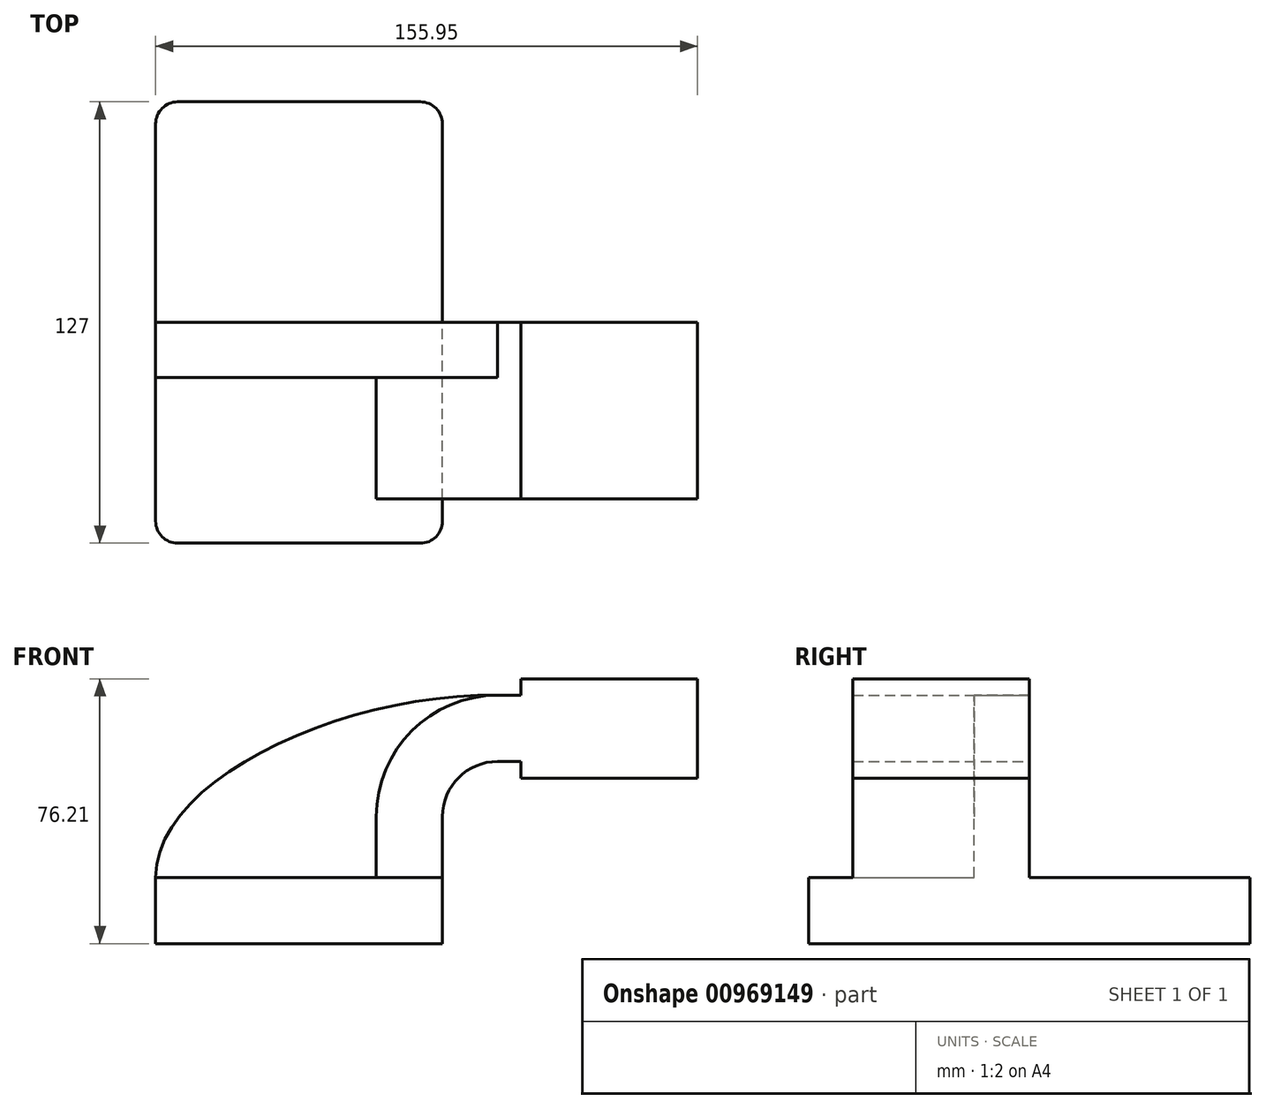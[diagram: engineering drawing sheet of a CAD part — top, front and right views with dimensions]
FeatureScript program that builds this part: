
annotation { "Feature Type Name" : "Feature", "Feature Type Description" : "" }
export const myFeature = defineFeature(function(context is Context, id is Id, definition is map)
    precondition{}
    {
        {
            var Q0;
            Q0=qCreatedBy(makeId("Front.planeOp"),FACE);
            var sketch = newSketch(context, id + "F0", { "sketchPlane" : qUnion([Q0])});
            skLineSegment(sketch, "E0.bottom", {"start": v(-41.27, -9.53) * mm, "end": v(41.28, -9.53) * mm});
            skLineSegment(sketch, "E0.top", {"start": v(-41.28, 9.53) * mm, "end": v(41.28, 9.53) * mm});
            skLineSegment(sketch, "E0.left", {"start": v(-41.28, -9.53) * mm, "end": v(-41.28, 9.53) * mm});
            skLineSegment(sketch, "E0.right", {"start": v(41.28, -9.53) * mm, "end": v(41.28, 9.52) * mm});
            skPoint(sketch, "E0.middle", {"position": v(0, 0) * mm});
            skLineSegment(sketch, "E1.bottom", {"start": v(63.87, 38.1) * mm, "end": v(114.67, 38.1) * mm});
            skLineSegment(sketch, "E1.top", {"start": v(63.87, 66.68) * mm, "end": v(114.67, 66.68) * mm});
            skLineSegment(sketch, "E1.left", {"start": v(63.87, 38.1) * mm, "end": v(63.87, 66.68) * mm});
            skLineSegment(sketch, "E1.right", {"start": v(114.67, 38.1) * mm, "end": v(114.67, 66.68) * mm});
            skPoint(sketch, "E1.middle", {"position": v(89.27, 52.39) * mm});
            skLineSegment(sketch, "E2", {"start": v(41.28, 9.52) * mm, "end": v(41.28, 27) * mm});
            skArc(sketch, "E3", {"start": v(41.27, 27) * mm, "mid": v(45.92, 38.23) * mm, "end": v(57.15, 42.88) * mm});
            skLineSegment(sketch, "E4", {"start": v(57.15, 42.88) * mm, "end": v(89.27, 42.88) * mm});
            skArc(sketch, "E5.0", {"start": v(53.97, 27) * mm, "mid": v(54.9, 29.25) * mm, "end": v(57.15, 30.18) * mm});
            skLineSegment(sketch, "E6.0", {"start": v(57.15, 61.93) * mm, "end": v(89.27, 61.93) * mm});
            skArc(sketch, "E6.1", {"start": v(22.22, 27) * mm, "mid": v(32.45, 51.7) * mm, "end": v(57.15, 61.93) * mm});
            skLineSegment(sketch, "E6.2", {"start": v(22.22, 9.52) * mm, "end": v(22.22, 27) * mm});
            skLineSegment(sketch, "E7", {"start": v(89.27, 66.68) * mm, "end": v(89.27, 38.1) * mm});
            skFitSpline(sketch, "E8", {"points": [v(-41.28, 9.53) * mm, v(57.15, 61.93) * mm], "startDerivative": vector(0.5, 85.92) * mm, "endDerivative": vector(132.47, -2.09) * mm});
            skPoint(sketch, "E9", {"position": v(114.67, 52.39) * mm});
            skPoint(sketch, "E10", {"position": v(63.87, 52.39) * mm});
            skSolve(sketch);
        }
        {
            var Q0;
            Q0=makeQuery(id+"F0.imprint","IMPRINT",FACE,{"disambiguationData":[TD([[makeQuery(id+"F0.imprint","IMPRINT",EDGE,{"derivedFrom":sQuery(id+"F0.wireOp",EDGE,"E0.bottom")}),1.0]])]});
            extrude(context, id + "F1", {"entities" : qUnion([Q0]), "endBound" : BoundingType.SYMMETRIC, "depth" : 127 * mm, "offsetDistance" : 25.4 * mm});
        }
        {
            var Q0;
            {var subQ1=sQuery(id+"F0.wireOp",EDGE,"E2");Q0=makeQuery(id+"F0.imprint","IMPRINT",FACE,{"disambiguationData":[TD([[makeQuery(id+"F0.imprint","IMPRINT",EDGE,{"derivedFrom":subQ1}),1.0]])]});}
            extrude(context, id + "F2", {"entities" : qUnion([Q0]), "operationType" : NewBodyOperationType.ADD, "depth" : 50.8 * mm, "offsetDistance" : 25.4 * mm});
        }
        {
            var Q0;
            {var subQ0=sQuery(id+"F0.wireOp",EDGE,"E4");var subQ1=sQuery(id+"F0.wireOp",EDGE,"E1.left");var subQ2=makeQuery(id+"F0.imprint","INTERSECT",VERTEX,{"derivedFrom":[subQ1,subQ0]});Q0=makeQuery(id+"F0.imprint","IMPRINT",FACE,{"disambiguationData":[TD([[makeQuery(id+"F0.imprint","IMPRINT",EDGE,{"disambiguationData":[TD([[subQ2,-1.0]])],"derivedFrom":subQ1}),-1.0]])]});}
            var Q1;
            {var subQ0=sQuery(id+"F0.wireOp",EDGE,"E1.right");Q1=makeQuery(id+"F0.imprint","IMPRINT",FACE,{"disambiguationData":[TD([[makeQuery(id+"F0.imprint","IMPRINT",EDGE,{"derivedFrom":subQ0}),1.0]])]});}
            var Q2;
            {var subQ0=sQuery(id+"F0.wireOp",EDGE,"E1.left");var subQ1=sQuery(id+"F0.wireOp",EDGE,"E1.top");var subQ2=makeQuery(id+"F0.imprint","INTERSECT",VERTEX,{"derivedFrom":[subQ1,subQ0]});Q2=makeQuery(id+"F0.imprint","IMPRINT",FACE,{"disambiguationData":[TD([[makeQuery(id+"F0.imprint","IMPRINT",EDGE,{"disambiguationData":[TD([[subQ2,-1.0]])],"derivedFrom":subQ1}),-1.0]])]});}
            var Q3;
            {var subQ0=sQuery(id+"F0.wireOp",EDGE,"E1.left");var subQ1=sQuery(id+"F0.wireOp",EDGE,"E1.bottom");var subQ2=makeQuery(id+"F0.imprint","INTERSECT",VERTEX,{"derivedFrom":[subQ1,subQ0]});Q3=makeQuery(id+"F0.imprint","IMPRINT",FACE,{"disambiguationData":[TD([[makeQuery(id+"F0.imprint","IMPRINT",EDGE,{"disambiguationData":[TD([[subQ2,-1.0]])],"derivedFrom":subQ1}),1.0]])]});}
            extrude(context, id + "F3", {"entities" : qUnion([Q0, Q1, Q2, Q3]), "operationType" : NewBodyOperationType.ADD, "depth" : 50.8 * mm, "offsetDistance" : 25.4 * mm});
        }
        {
            var Q0;
            Q0 = qSketchRegion(id + "F0", true);
            extrude(context, id + "F4", {"entities" : qUnion([Q0]), "operationType" : NewBodyOperationType.ADD, "depth" : 15.88 * mm, "offsetDistance" : 25.4 * mm});
        }
        {
            var Q0;
            Q0=makeQuery(id+"F1.opExtrude","CAP_EDGE",EDGE,{"disambiguationData":[OSD([sQuery(id+"F0.wireOp",EDGE,"E0.right")])],"isStart":false});
            var Q1;
            Q1=makeQuery(id+"F1.opExtrude","CAP_EDGE",EDGE,{"disambiguationData":[OSD([sQuery(id+"F0.wireOp",EDGE,"E0.left")])],"isStart":false});
            var Q2;
            Q2=makeQuery(id+"F1.opExtrude","CAP_EDGE",EDGE,{"disambiguationData":[OSD([sQuery(id+"F0.wireOp",EDGE,"E0.right")])],"isStart":true});
            var Q3;
            Q3=makeQuery(id+"F1.opExtrude","CAP_EDGE",EDGE,{"disambiguationData":[OSD([sQuery(id+"F0.wireOp",EDGE,"E0.left")])],"isStart":true});
            fillet(context, id + "F5", {"entities" : qUnion([Q0, Q1, Q2, Q3]), "radius" : 6.35 * mm, "tangentPropagation" : true, "allowEdgeOverflow" : false});
        }
    });
